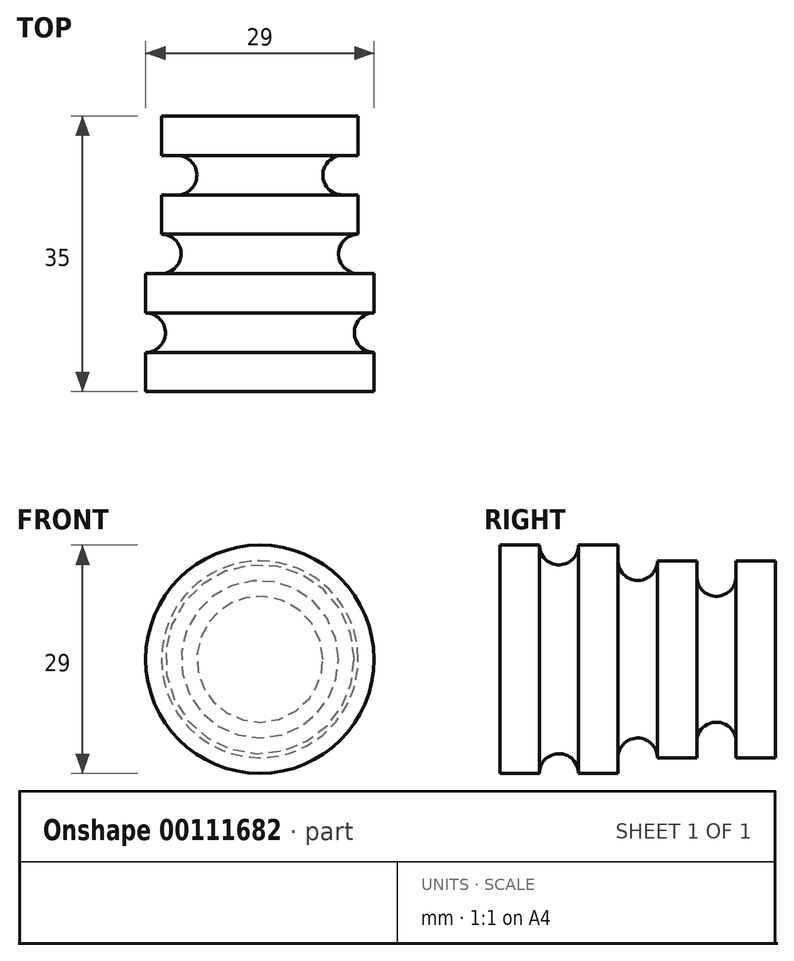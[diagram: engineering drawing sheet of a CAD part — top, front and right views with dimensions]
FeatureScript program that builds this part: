
annotation { "Feature Type Name" : "Feature", "Feature Type Description" : "" }
export const myFeature = defineFeature(function(context is Context, id is Id, definition is map)
    precondition{}
    {
        {
            var Q0;
            Q0=qCreatedBy(makeId("Top.planeOp"),FACE);
            var sketch = newSketch(context, id + "F0", { "sketchPlane" : qUnion([Q0])});
            skLineSegment(sketch, "E0.bottom", {"start": v(-11.12, -14.22) * mm, "end": v(3.38, -14.22) * mm});
            skLineSegment(sketch, "E0.top", {"start": v(-11.12, -9.22) * mm, "end": v(3.38, -9.22) * mm});
            skLineSegment(sketch, "E0.left", {"start": v(-11.12, -14.22) * mm, "end": v(-11.12, -9.22) * mm});
            skLineSegment(sketch, "E0.right", {"start": v(3.38, -14.22) * mm, "end": v(3.38, -9.22) * mm});
            skLineSegment(sketch, "E1.bottom", {"start": v(3.38, -9.22) * mm, "end": v(-8.62, -9.22) * mm});
            skLineSegment(sketch, "E1.top", {"start": v(3.38, -4.22) * mm, "end": v(-8.62, -4.22) * mm});
            skLineSegment(sketch, "E1.left", {"start": v(3.38, -9.22) * mm, "end": v(3.38, -4.22) * mm});
            skLineSegment(sketch, "E1.right", {"start": v(-8.62, -9.22) * mm, "end": v(-8.62, -4.22) * mm});
            skLineSegment(sketch, "E2.bottom", {"start": v(3.38, -4.22) * mm, "end": v(-11.12, -4.22) * mm});
            skLineSegment(sketch, "E2.top", {"start": v(3.38, 0.78) * mm, "end": v(-11.12, 0.78) * mm});
            skLineSegment(sketch, "E2.left", {"start": v(3.38, -4.22) * mm, "end": v(3.38, 0.78) * mm});
            skLineSegment(sketch, "E2.right", {"start": v(-11.12, -4.22) * mm, "end": v(-11.12, 0.78) * mm});
            skLineSegment(sketch, "E3.bottom", {"start": v(3.38, 0.78) * mm, "end": v(-6.62, 0.78) * mm});
            skLineSegment(sketch, "E3.top", {"start": v(3.38, 5.78) * mm, "end": v(-6.62, 5.78) * mm});
            skLineSegment(sketch, "E3.left", {"start": v(3.38, 0.78) * mm, "end": v(3.38, 5.78) * mm});
            skLineSegment(sketch, "E3.right", {"start": v(-6.62, 0.78) * mm, "end": v(-6.62, 5.78) * mm});
            skLineSegment(sketch, "E4.bottom", {"start": v(3.38, 5.78) * mm, "end": v(-9.12, 5.78) * mm});
            skLineSegment(sketch, "E4.top", {"start": v(3.38, 10.78) * mm, "end": v(-9.12, 10.78) * mm});
            skLineSegment(sketch, "E4.left", {"start": v(3.38, 5.78) * mm, "end": v(3.38, 10.78) * mm});
            skLineSegment(sketch, "E4.right", {"start": v(-9.12, 5.78) * mm, "end": v(-9.12, 10.78) * mm});
            skLineSegment(sketch, "E5.bottom", {"start": v(3.38, 10.78) * mm, "end": v(-4.62, 10.78) * mm});
            skLineSegment(sketch, "E5.top", {"start": v(3.38, 15.78) * mm, "end": v(-4.62, 15.78) * mm});
            skLineSegment(sketch, "E5.left", {"start": v(3.38, 10.78) * mm, "end": v(3.38, 15.78) * mm});
            skLineSegment(sketch, "E5.right", {"start": v(-4.62, 10.78) * mm, "end": v(-4.62, 15.78) * mm});
            skLineSegment(sketch, "E6.bottom", {"start": v(3.38, 15.78) * mm, "end": v(-9.12, 15.78) * mm});
            skLineSegment(sketch, "E6.top", {"start": v(3.38, 20.78) * mm, "end": v(-9.12, 20.78) * mm});
            skLineSegment(sketch, "E6.left", {"start": v(3.38, 15.78) * mm, "end": v(3.38, 20.78) * mm});
            skLineSegment(sketch, "E6.right", {"start": v(-9.12, 15.78) * mm, "end": v(-9.12, 20.78) * mm});
            skSolve(sketch);
        }
        {
            var Q0;
            Q0 = qSketchRegion(id + "F0", true);
            var Q1;
            Q1=sQuery(id+"F0.wireOp",EDGE,"E3.left");
            revolve(context, id + "F1", {"entities" : qUnion([Q0]), "axis" : qUnion([Q1]), "revolveType" : RevolveType.FULL});
        }
        {
            var Q0;
            Q0=makeQuery(id+"F1.opRevolve","SWEPT_EDGE",EDGE,{"disambiguationData":[OSD([sQuery(id+"F0.wireOp",EDGE,"E5.right"),sQuery(id+"F0.wireOp",EDGE,"E6.bottom")])]});
            var Q1;
            Q1=makeQuery(id+"F1.opRevolve","SWEPT_EDGE",EDGE,{"disambiguationData":[OSD([sQuery(id+"F0.wireOp",EDGE,"E4.top"),sQuery(id+"F0.wireOp",EDGE,"E5.bottom"),sQuery(id+"F0.wireOp",EDGE,"E5.right")])]});
            var Q2;
            Q2=makeQuery(id+"F1.opRevolve","SWEPT_EDGE",EDGE,{"disambiguationData":[OSD([sQuery(id+"F0.wireOp",EDGE,"E3.right"),sQuery(id+"F0.wireOp",EDGE,"E4.bottom")])]});
            var Q3;
            Q3=makeQuery(id+"F1.opRevolve","SWEPT_EDGE",EDGE,{"disambiguationData":[OSD([sQuery(id+"F0.wireOp",EDGE,"E2.top"),sQuery(id+"F0.wireOp",EDGE,"E3.bottom"),sQuery(id+"F0.wireOp",EDGE,"E3.right")])]});
            var Q4;
            Q4=makeQuery(id+"F1.opRevolve","SWEPT_EDGE",EDGE,{"disambiguationData":[OSD([sQuery(id+"F0.wireOp",EDGE,"E1.right"),sQuery(id+"F0.wireOp",EDGE,"E2.bottom")])]});
            var Q5;
            Q5=makeQuery(id+"F1.opRevolve","SWEPT_EDGE",EDGE,{"disambiguationData":[OSD([sQuery(id+"F0.wireOp",EDGE,"E0.top"),sQuery(id+"F0.wireOp",EDGE,"E1.bottom"),sQuery(id+"F0.wireOp",EDGE,"E1.right")])]});
            fillet(context, id + "F2", {"entities" : qUnion([Q0, Q1, Q2, Q3, Q4, Q5]), "radius" : 2.5 * mm, "tangentPropagation" : true, "allowEdgeOverflow" : false});
        }
    });
